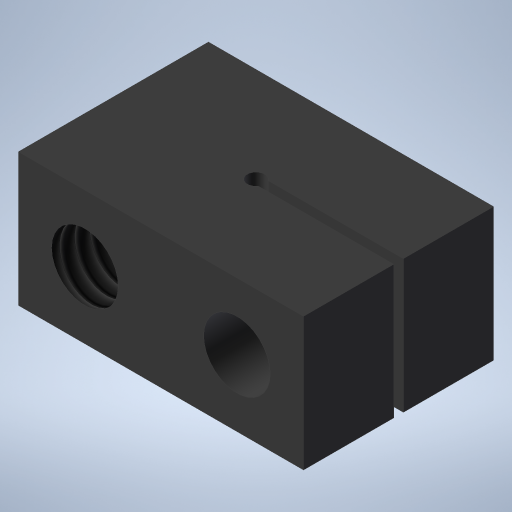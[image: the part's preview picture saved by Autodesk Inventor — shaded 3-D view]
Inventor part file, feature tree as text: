
AUTODESK INVENTOR PART (.ipt)
format: ipt  version: 2024 (Build 280153000, 153)  size: 220,672 bytes
history: native  units: in
note: dims shown in document units (in); Inventor stores cm internally (conversion verified against a paired STEP export)
features: sketch x3, extrude x2, hole x2, thread x2
ambient origin geometry x8: Origin, YZ Plane, XZ Plane, XY Plane, X Axis, Y Axis, Z Axis, Center Point
bodies: Solid1 (feature_tree)
feature tree (9):
  extrude  "Extrusion1"  Depth=0.3937in
  sketch  "Sketch2"  dims[d2=0.2953in d3=0.036in]
  hole  "Hole1"  [1 undecoded]
  hole  "Hole2"  [1 undecoded]
  thread  "Thread1"  [1 undecoded]
  thread  "Thread2"  [1 undecoded]
  extrude  "Extrusion2"  Depth=0.3937in
  sketch  "Sketch1"  dims[d0=0.5906in d1=0.3937in]
  sketch  "Sketch3"  dims[d4=0.01in d5=0.01in d6=0.2756in d7=0.0in d8=135.0deg d9=0.138in d10=45.0deg d11=0.138in d12=0.138in d13=0.75in d14=0.375in d15=0.25in d16=0.5635in d17=1.0in d18=0.8108in d19=0.138in d20=0.75in d21=0.375in d22=0.25in d23=0.5635in d24=1.0in d25=0.8108in d26=0.3937in d27=0.0in d28=0.1809in d29=0.0in d30=0.04in d31=0.1378in d32=0.0in]
note: 4 required parameter values undecoded (feature->parameter linkage not recoverable at this tier; creation-order binding heuristic only, values carry confidence <= 0.55)
